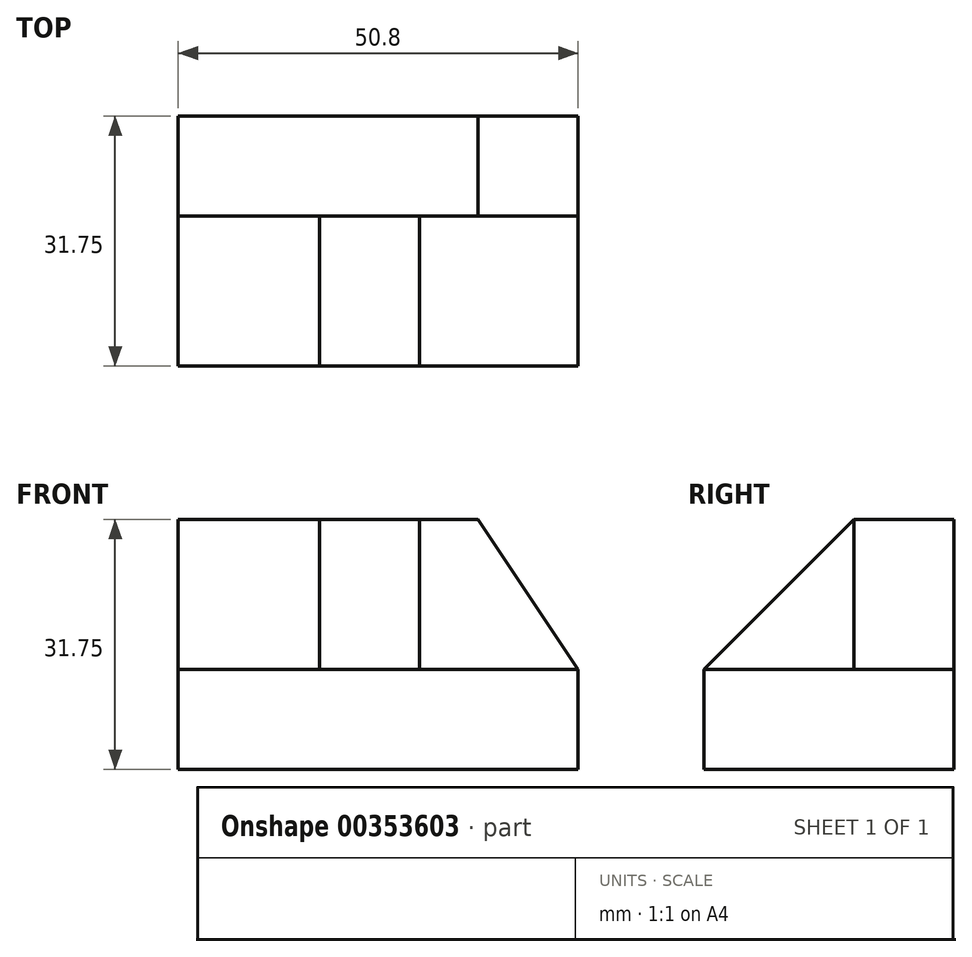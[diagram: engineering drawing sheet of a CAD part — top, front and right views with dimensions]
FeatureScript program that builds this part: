
annotation { "Feature Type Name" : "Feature", "Feature Type Description" : "" }
export const myFeature = defineFeature(function(context is Context, id is Id, definition is map)
    precondition{}
    {
        {
            var Q0;
            Q0=qCreatedBy(makeId("Right.planeOp"),FACE);
            var sketch = newSketch(context, id + "F0", { "sketchPlane" : qUnion([Q0])});
            skLineSegment(sketch, "E0", {"start": v(0, 0) * mm, "end": v(0, 31.75) * mm});
            skLineSegment(sketch, "E1", {"start": v(0, 31.75) * mm, "end": v(-12.7, 31.75) * mm});
            skLineSegment(sketch, "E2", {"start": v(-12.7, 31.75) * mm, "end": v(-12.7, 12.7) * mm});
            skLineSegment(sketch, "E3", {"start": v(-12.7, 12.7) * mm, "end": v(-31.75, 12.7) * mm});
            skLineSegment(sketch, "E4", {"start": v(-31.75, 12.7) * mm, "end": v(-31.75, 0) * mm});
            skLineSegment(sketch, "E5", {"start": v(-31.75, 0) * mm, "end": v(0, 0) * mm});
            skSolve(sketch);
        }
        {
            var Q0;
            Q0=makeQuery(id+"F0.imprint","IMPRINT",FACE,{"disambiguationData":[TD([[makeQuery(id+"F0.imprint","IMPRINT",EDGE,{"derivedFrom":sQuery(id+"F0.wireOp",EDGE,"E0")}),1.0]])]});
            extrude(context, id + "F1", {"entities" : qUnion([Q0]), "depth" : 50.8 * mm});
        }
        {
            var Q0;
            Q0=makeQuery(id+"F1.opExtrude","SWEPT_FACE",FACE,{"disambiguationData":[OSD([sQuery(id+"F0.wireOp",EDGE,"E2")])]});
            var sketch = newSketch(context, id + "F2", { "sketchPlane" : qUnion([Q0])});
            skLineSegment(sketch, "E6", {"start": v(50.8, 12.7) * mm, "end": v(38.1, 31.75) * mm});
            skLineSegment(sketch, "E7", {"start": v(38.1, 31.75) * mm, "end": v(50.8, 31.75) * mm});
            skLineSegment(sketch, "E8", {"start": v(50.8, 31.75) * mm, "end": v(50.8, 12.7) * mm});
            skSolve(sketch);
        }
        {
            var Q0;
            Q0=makeQuery(id+"F2.imprint","IMPRINT",FACE,{"disambiguationData":[TD([[makeQuery(id+"F2.imprint","IMPRINT",EDGE,{"derivedFrom":sQuery(id+"F2.wireOp",EDGE,"E6")}),-1.0]])]});
            extrude(context, id + "F3", {"entities" : qUnion([Q0]), "operationType" : NewBodyOperationType.REMOVE, "oppositeDirection" : true, "depth" : 37.08 * mm});
        }
        {
            var Q0;
            Q0=makeQuery(id+"F1.opExtrude","SWEPT_FACE",FACE,{"disambiguationData":[OSD([sQuery(id+"F0.wireOp",EDGE,"E3")])]});
            var sketch = newSketch(context, id + "F4", { "sketchPlane" : qUnion([Q0])});
            skLineSegment(sketch, "E9", {"start": v(17.97, -12.7) * mm, "end": v(30.67, -12.7) * mm});
            skLineSegment(sketch, "E10", {"start": v(30.67, -12.7) * mm, "end": v(30.67, -31.75) * mm});
            skLineSegment(sketch, "E11", {"start": v(30.67, -31.75) * mm, "end": v(17.97, -31.75) * mm});
            skLineSegment(sketch, "E12", {"start": v(17.97, -31.75) * mm, "end": v(17.97, -12.7) * mm});
            skSolve(sketch);
        }
        {
            var Q0;
            Q0=makeQuery(id+"F4.imprint","IMPRINT",FACE,{"disambiguationData":[TD([[makeQuery(id+"F4.imprint","IMPRINT",EDGE,{"derivedFrom":sQuery(id+"F4.wireOp",EDGE,"E9")}),1.0]])]});
            extrude(context, id + "F5", {"entities" : qUnion([Q0]), "operationType" : NewBodyOperationType.ADD, "depth" : 19.05 * mm});
        }
        {
            var Q0;
            Q0=makeQuery(id+"F5.opExtrude","SWEPT_FACE",FACE,{"disambiguationData":[OSD([sQuery(id+"F4.wireOp",EDGE,"E10")])]});
            var sketch = newSketch(context, id + "F6", { "sketchPlane" : qUnion([Q0])});
            skLineSegment(sketch, "E13", {"start": v(-31.75, 12.7) * mm, "end": v(-12.7, 31.75) * mm});
            skLineSegment(sketch, "E14", {"start": v(-12.7, 31.75) * mm, "end": v(-31.75, 31.75) * mm});
            skLineSegment(sketch, "E15", {"start": v(-31.75, 31.75) * mm, "end": v(-31.75, 12.7) * mm});
            skSolve(sketch);
        }
        {
            var Q0;
            Q0=makeQuery(id+"F6.imprint","IMPRINT",FACE,{"disambiguationData":[TD([[makeQuery(id+"F6.imprint","IMPRINT",EDGE,{"derivedFrom":sQuery(id+"F6.wireOp",EDGE,"E13")}),1.0]])]});
            extrude(context, id + "F7", {"entities" : qUnion([Q0]), "operationType" : NewBodyOperationType.REMOVE, "oppositeDirection" : true, "depth" : 25.4 * mm});
        }
    });
